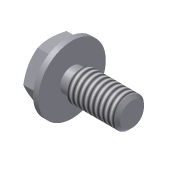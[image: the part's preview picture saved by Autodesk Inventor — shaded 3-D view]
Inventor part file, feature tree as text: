
AUTODESK INVENTOR PART (.ipt)
format: ipt  version: 2019 (Build 230136000, 136)  size: 262,656 bytes
history: native  units: mm (DEFAULTED — no unit token found)
features: sketch x2, extrude x1, chamfer x1, plane x1
ambient origin geometry x7: Origin, YZ Plane, XZ Plane, X Axis, Y Axis, Z Axis, Center Point
bodies: Solid1 (feature_tree), Body (feature_tree)
feature tree (5):
  extrude  "Head"  Depth=5.0mm
  chamfer  "Chamfer1"  Angle=90.0deg  [1 undecoded]
  plane  "Work Plane1"
  sketch  "Sketch1"  dims[d0=6.0mm d1=5.0mm]
  sketch  "Sketch2"  dims[d2=3.0mm d12=90.0deg d3=2.36mm d4=0.0mm d5=30.0deg d21=90.0deg d6=0.306725mm d7=0.306825mm d8=0.53mm d9=6.75mm d10=5.0mm d13=5.0mm d14=0.0mm d15=2.38655mm d16=0.306725mm d17=0.0mm d18=4.5mm d41=45.0deg d42=0.0mm d43=0.0mm]
note: 1 required parameter value undecoded (feature->parameter linkage not recoverable at this tier; creation-order binding heuristic only, values carry confidence <= 0.55)
